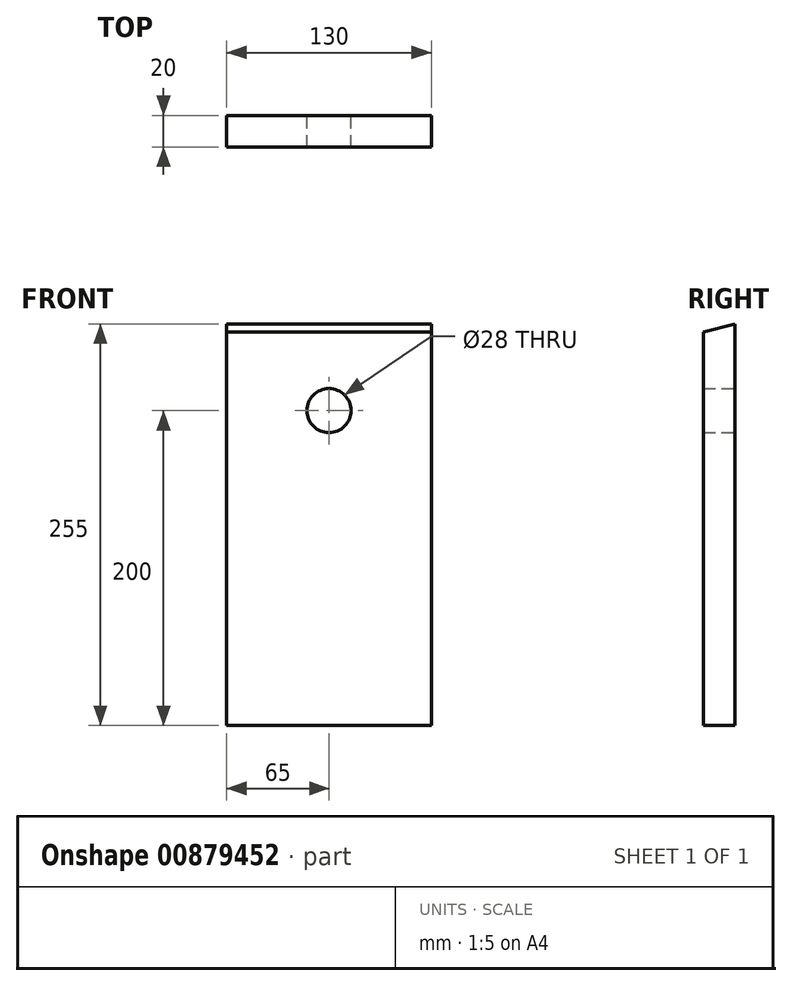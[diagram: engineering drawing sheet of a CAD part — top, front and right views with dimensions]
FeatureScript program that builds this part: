
annotation { "Feature Type Name" : "Feature", "Feature Type Description" : "" }
export const myFeature = defineFeature(function(context is Context, id is Id, definition is map)
    precondition{}
    {
        {
            var Q0;
            Q0=qCreatedBy(makeId("Front.planeOp"),FACE);
            var sketch = newSketch(context, id + "F0", { "sketchPlane" : qUnion([Q0])});
            skLineSegment(sketch, "E0.bottom", {"start": v(65, 125) * mm, "end": v(-65, 125) * mm});
            skLineSegment(sketch, "E0.top", {"start": v(65, -125) * mm, "end": v(-65, -125) * mm});
            skLineSegment(sketch, "E0.left", {"start": v(65, 125) * mm, "end": v(65, -125) * mm});
            skLineSegment(sketch, "E0.right", {"start": v(-65, 125) * mm, "end": v(-65, -125) * mm});
            skPoint(sketch, "E0.middle", {"position": v(0, 0) * mm});
            skCircle(sketch, "E1", {"center": v(0, 75) * mm, "radius": 14 * mm});
            skPoint(sketch, "E2", {"position": v(0, 125) * mm});
            skSolve(sketch);
        }
        {
            var Q0;
            Q0=makeQuery(id+"F0.imprint","IMPRINT",FACE,{"disambiguationData":[TD([[makeQuery(id+"F0.imprint","IMPRINT",EDGE,{"derivedFrom":sQuery(id+"F0.wireOp",EDGE,"E0.bottom")}),1.0]])]});
            extrude(context, id + "F1", {"entities" : qUnion([Q0]), "endBound" : BoundingType.SYMMETRIC, "depth" : 20 * mm, "offsetDistance" : 25 * mm});
        }
        {
            var Q0;
            Q0=makeQuery(id+"F1.opExtrude","SWEPT_FACE",FACE,{"disambiguationData":[OSD([sQuery(id+"F0.wireOp",EDGE,"E0.left")])]});
            var sketch = newSketch(context, id + "F2", { "sketchPlane" : qUnion([Q0])});
            skCircle(sketch, "E3", {"center": v(0, -95) * mm, "radius": 5 * mm});
            skPoint(sketch, "E3.centerSnap0", {"position": v(0, -125) * mm});
            skLineSegment(sketch, "E4", {"start": v(-10, 0) * mm, "end": v(10, 0) * mm, "construction": true});
            skCircle(sketch, "E5.MirrorC", {"center": v(0, 115) * mm, "radius": 5 * mm});
            skSolve(sketch);
        }
        {
            var Q0;
            Q0=makeQuery(id+"F1.opExtrude","SWEPT_FACE",FACE,{"disambiguationData":[OSD([sQuery(id+"F0.wireOp",EDGE,"E0.right")])]});
            var sketch = newSketch(context, id + "F3", { "sketchPlane" : qUnion([Q0])});
            skCircle(sketch, "E6", {"center": v(0, -95) * mm, "radius": 5 * mm});
            skPoint(sketch, "E6.centerSnap0", {"position": v(0, -125) * mm});
            skLineSegment(sketch, "E7", {"start": v(-10, 0) * mm, "end": v(10, 0) * mm, "construction": true});
            skCircle(sketch, "E8.MirrorC", {"center": v(0, 115) * mm, "radius": 5 * mm});
            skSolve(sketch);
        }
        {
            var Q0;
            Q0=makeQuery(id+"F1.opExtrude","SWEPT_FACE",FACE,{"disambiguationData":[OSD([sQuery(id+"F0.wireOp",EDGE,"E0.left")])]});
            var sketch = newSketch(context, id + "F4", { "sketchPlane" : qUnion([Q0])});
            skLineSegment(sketch, "E9", {"start": v(10, 125) * mm, "end": v(10, 130) * mm});
            skLineSegment(sketch, "E10", {"start": v(-10, 125) * mm, "end": v(10, 130) * mm});
            skSolve(sketch);
        }
        {
            var Q0;
            Q0=makeQuery(id+"F4.imprint","IMPRINT",FACE,{"disambiguationData":[TD([[makeQuery(id+"F4.imprint","IMPRINT",EDGE,{"derivedFrom":sQuery(id+"F4.wireOp",EDGE,"E9")}),1.0]])]});
            extrude(context, id + "F5", {"entities" : qUnion([Q0]), "operationType" : NewBodyOperationType.ADD, "oppositeDirection" : true, "depth" : 130 * mm, "offsetDistance" : 25 * mm});
        }
    });
